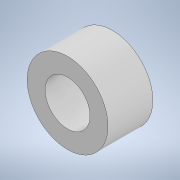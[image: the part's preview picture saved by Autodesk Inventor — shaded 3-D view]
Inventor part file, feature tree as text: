
AUTODESK INVENTOR PART (.ipt)
format: ipt  version: 2020 (Build 240168000, 168)  size: 100,352 bytes
history: native  units: in
note: dims shown in document units (in); Inventor stores cm internally (conversion verified against a paired STEP export)
features: extrude x2, sketch x2
ambient origin geometry x8: Origin, YZ Plane, XZ Plane, XY Plane, X Axis, Y Axis, Z Axis, Center Point
bodies: Solid1 (feature_tree)
feature tree (4):
  extrude  "Extrusion1"  Depth=0.25in TaperAngle=0.0deg
  extrude  "Extrusion2"  Depth=0.25in TaperAngle=0.0deg
  sketch  "Sketch1"  dims[d0=0.45in d1=0.25in d2=0.0in]
  sketch  "Sketch2"  dims[d3=0.25in d4=0.25in d5=0.0in]
